# Revit family: MBS_table
name_source: partatom
category: Generic Models
revit_build: Autodesk Revit 2014 (Build: 20130308_1515(x64)
units: mm (PartAtom-declared; Revit-internal decimal feet)

## types (3) — shared parameters
support material = Laminate, Ivory, Matte TABLE SUPPORT MBS
thickness = 50 mm  [stored 0.164042 ft]

## per-type parameters (varying)
| type | c_side height | c_side widht | c_support widht | c_table depht | c_table height | c_table widht |
| table | 630 mm  [stored 2.06693 ft] | 1200 mm | 150 mm | 1200 mm | 750 mm  [stored 2.46063 ft] | 2250 mm |
| stool | 500 mm  [stored 1.64042 ft] | 350 mm  [stored 1.14829 ft] | 50 mm  [stored 0.164042 ft] | 350 mm  [stored 1.14829 ft] | 600 mm | 450 mm  [stored 1.47638 ft] |
| desk | 650 mm  [stored 2.13255 ft] | 750 mm  [stored 2.46063 ft] | 100 mm  [stored 0.328084 ft] | 750 mm  [stored 2.46063 ft] | 750 mm  [stored 2.46063 ft] | 1500 mm  [stored 4.92126 ft] |

note: [stored X ft] marks values corroborated as IEEE doubles in the binary element streams (Revit-internal decimal feet)

## geometry (parser evidence)
native form markers: Sweep x1
no freeform markers — native parametric forms only
